FCSTD DOCUMENT  (FreeCAD 0.22R37543 (Git))
Label: FreeCAD_Symbol
License: All rights reserved
LicenseURL: https://en.wikipedia.org/wiki/All_rights_reserved
objects: Sketcher::SketchObject×1
note: 1 computed .brp shape members not serialized (recipe doc carries the construction recipe); baked Part::Feature solids carry a one-line shape summary decoded from their .brp

FEATURE [Sketcher::SketchObject] Sketch001  label="Logo_Sketch"
  FullyConstrained = true
  sketch-geometry (64):
    g0: LineSegment StartX=0 StartY=-4 StartZ=0 EndX=0 EndY=-24 EndZ=0
    g1: LineSegment StartX=0 StartY=-24 StartZ=0 EndX=8.05 EndY=-24 EndZ=0
    g2: LineSegment StartX=20 StartY=-7.99606 StartZ=0 EndX=20 EndY=0 EndZ=0
    g3: LineSegment StartX=20 StartY=0 StartZ=0 EndX=4 EndY=0 EndZ=0
    g4: ArcOfCircle CenterX=4 CenterY=-4 CenterZ=0 NormalX=0 NormalY=0 NormalZ=1 AngleXU=0 Radius=4 StartAngle=1.5708 EndAngle=3.14159
    g5: GeomPoint X=0 Y=0 Z=0
    g6: LineSegment StartX=4 StartY=0 StartZ=0 EndX=0 EndY=-4 EndZ=0
    g7: LineSegment StartX=4 StartY=-4 StartZ=0 EndX=4 EndY=-20 EndZ=0
    g8: LineSegment StartX=4 StartY=-20 StartZ=0 EndX=8 EndY=-20 EndZ=0
    g9: LineSegment StartX=8 StartY=-20 StartZ=0 EndX=8 EndY=-15 EndZ=0
    g10: LineSegment StartX=8 StartY=-15 StartZ=0 EndX=12 EndY=-15 EndZ=0
    g11: LineSegment StartX=12 StartY=-15 StartZ=0 EndX=12 EndY=-11 EndZ=0
    g12: LineSegment StartX=12 StartY=-11 StartZ=0 EndX=8 EndY=-11 EndZ=0
    g13: LineSegment StartX=8 StartY=-11 StartZ=0 EndX=8 EndY=-8 EndZ=0
    g14: LineSegment StartX=8 StartY=-8 StartZ=0 EndX=16 EndY=-8 EndZ=0
    g15: LineSegment StartX=16 StartY=-8 StartZ=0 EndX=16 EndY=-4 EndZ=0
    g16: LineSegment StartX=16 StartY=-4 StartZ=0 EndX=4 EndY=-4 EndZ=0
    g17: LineSegment StartX=19.7114 StartY=-8.56237 StartZ=0 EndX=17.5386 EndY=-10.1411 EndZ=0
    g18: LineSegment StartX=17.25 StartY=-10.7074 StartZ=0 EndX=17.25 EndY=-11.2926 EndZ=0
    g19: LineSegment StartX=17.5386 StartY=-11.8589 StartZ=0 EndX=19.4339 EndY=-13.236 EndZ=0
    g20: LineSegment StartX=19.6882 StartY=-14.0186 StartZ=0 EndX=19.0393 EndY=-16.0158 EndZ=0
    g21: LineSegment StartX=18.3735 StartY=-16.4995 StartZ=0 EndX=16.0307 EndY=-16.4995 EndZ=0
    g22: LineSegment StartX=15.4644 StartY=-16.7881 StartZ=0 EndX=15.1204 EndY=-17.2615 EndZ=0
    g23: LineSegment StartX=15.021 StartY=-17.8893 StartZ=0 EndX=15.745 EndY=-20.1174 EndZ=0
    g24: LineSegment StartX=15.4907 StartY=-20.9 StartZ=0 EndX=13.7917 EndY=-22.1344 EndZ=0
    g25: LineSegment StartX=12.9688 StartY=-22.1344 StartZ=0 EndX=11.0735 EndY=-20.7573 EndZ=0
    g26: LineSegment StartX=10.4457 StartY=-20.6579 StartZ=0 EndX=9.88913 EndY=-20.8388 EndZ=0
    g27: LineSegment StartX=9.4397 StartY=-21.2882 StartZ=0 EndX=8.71574 EndY=-23.5163 EndZ=0
    g28: LineSegment StartX=7 StartY=-11 StartZ=0 EndX=19.3637 EndY=-15.0172 EndZ=0
    g29: LineSegment StartX=7 StartY=-11 StartZ=0 EndX=19.3637 EndY=-6.98278 EndZ=0
    g30: LineSegment StartX=7 StartY=-11 StartZ=0 EndX=14.6412 EndY=-21.5172 EndZ=0
    g31: LineSegment StartX=7 StartY=-11 StartZ=0 EndX=7 EndY=-24 EndZ=0
    g32: Circle CenterX=7 CenterY=-11 CenterZ=0 NormalX=0 NormalY=0 NormalZ=1 AngleXU=0 Radius=13
    g33: LineSegment StartX=7 StartY=-11 StartZ=0 EndX=20 EndY=-11 EndZ=0
    g34: LineSegment StartX=7 StartY=-11 StartZ=0 EndX=17.5172 EndY=-18.6412 EndZ=0
    g35: LineSegment StartX=7 StartY=-11 StartZ=0 EndX=11.0172 EndY=-23.3637 EndZ=0
    g36: GeomPoint X=10.1674 Y=-20.7483 Z=0
    g37: Circle CenterX=7 CenterY=-11 CenterZ=0 NormalX=0 NormalY=0 NormalZ=1 AngleXU=0 Radius=10.25
    g38: ArcOfCircle CenterX=19.3 CenterY=-7.99606 CenterZ=0 NormalX=0 NormalY=0 NormalZ=1 AngleXU=0 Radius=0.7 StartAngle=5.34071 EndAngle=6.28319
    g39: GeomPoint X=20 Y=-8.35273 Z=0
    g40: ArcOfCircle CenterX=19.0225 CenterY=-13.8023 CenterZ=0 NormalX=0 NormalY=0 NormalZ=1 AngleXU=0 Radius=0.7 StartAngle=5.96903 EndAngle=7.22566
    g41: GeomPoint X=19.8454 Y=-13.5349 Z=0
    g42: ArcOfCircle CenterX=17.95 CenterY=-11.2926 CenterZ=0 NormalX=0 NormalY=0 NormalZ=1 AngleXU=0 Radius=0.7 StartAngle=3.14159 EndAngle=4.08407
    g43: GeomPoint X=17.25 Y=-11.6493 Z=0
    g44: ArcOfCircle CenterX=17.95 CenterY=-10.7074 CenterZ=0 NormalX=0 NormalY=0 NormalZ=1 AngleXU=0 Radius=0.7 StartAngle=2.19911 EndAngle=3.14159
    g45: GeomPoint X=17.25 Y=-10.3507 Z=0
    g46: ArcOfCircle CenterX=18.3735 CenterY=-15.7995 CenterZ=0 NormalX=0 NormalY=0 NormalZ=1 AngleXU=0 Radius=0.7 StartAngle=4.71239 EndAngle=5.96903
    g47: GeomPoint X=18.8821 Y=-16.4995 Z=0
    g48: ArcOfCircle CenterX=16.0307 CenterY=-17.1995 CenterZ=0 NormalX=0 NormalY=0 NormalZ=1 AngleXU=0 Radius=0.7 StartAngle=1.5708 EndAngle=2.51327
    g49: GeomPoint X=15.6741 Y=-16.4995 Z=0
    g50: ArcOfCircle CenterX=15.6867 CenterY=-17.673 CenterZ=0 NormalX=0 NormalY=0 NormalZ=1 AngleXU=0 Radius=0.7 StartAngle=2.51327 EndAngle=3.45575
    g51: GeomPoint X=14.9108 Y=-17.5501 Z=0
    g52: ArcOfCircle CenterX=15.0792 CenterY=-20.3337 CenterZ=0 NormalX=0 NormalY=0 NormalZ=1 AngleXU=0 Radius=0.7 StartAngle=5.34071 EndAngle=6.59734
    g53: GeomPoint X=15.9021 Y=-20.6011 Z=0
    g54: ArcOfCircle CenterX=13.3803 CenterY=-21.5681 CenterZ=0 NormalX=0 NormalY=0 NormalZ=1 AngleXU=0 Radius=0.7 StartAngle=4.08407 EndAngle=5.34071
    g55: GeomPoint X=13.3803 Y=-22.4333 Z=0
    g56: ArcOfCircle CenterX=10.662 CenterY=-21.3236 CenterZ=0 NormalX=0 NormalY=0 NormalZ=1 AngleXU=0 Radius=0.7 StartAngle=0.942478 EndAngle=1.88496
    g57: GeomPoint X=10.7849 Y=-20.5477 Z=0
    g58: ArcOfCircle CenterX=10.1054 CenterY=-21.5045 CenterZ=0 NormalX=0 NormalY=0 NormalZ=1 AngleXU=0 Radius=0.7 StartAngle=1.88496 EndAngle=2.82743
    g59: GeomPoint X=9.54992 Y=-20.949 Z=0
    g60: ArcOfCircle CenterX=8.05 CenterY=-23.3 CenterZ=0 NormalX=0 NormalY=0 NormalZ=1 AngleXU=0 Radius=0.7 StartAngle=4.71239 EndAngle=5.96903
    g61: GeomPoint X=8.55858 Y=-24 Z=0
    g62: GeomPoint X=17.25 Y=-11 Z=0
    g63: GeomPoint X=15.2924 Y=-17.0248 Z=0
  constraints (153):
    c: Coincident(g0,g1)
    c: Coincident(g2,g3)
    c: Vertical(g0)
    c: Vertical(g2)
    c: Horizontal(g1)
    c: Horizontal(g3)
    c: Coincident(g5,g-1)
    c: DistanceY(g0,g5) = 24
    c: DistanceX(g5,g3) = 20
    c: PointOnObject(g5,g0)
    c: PointOnObject(g5,g3)
    c: Tangent(g0,g4) = -1.5708
    c: Tangent(g3,g4) = -1.5708
    c: Coincident(g6,g0)
    c: Coincident(g6,g3)
    c: DistanceX(g-1,g3) = 4
    c: Coincident(g7,g4)
    c: Vertical(g7)
    c: Coincident(g7,g8)
    c: Horizontal(g8)
    c: Coincident(g8,g9)
    c: Vertical(g9)
    c: Coincident(g9,g10)
    c: Coincident(g10,g11)
    c: Coincident(g11,g12)
    c: Coincident(g12,g13)
    c: Coincident(g13,g14)
    c: Coincident(g14,g15)
    c: Coincident(g15,g16)
    c: Coincident(g16,g7)
    c: Horizontal(g10)
    c: Vertical(g11)
    c: Horizontal(g12)
    c: Vertical(g13)
    c: Horizontal(g14)
    c: Vertical(g15)
    c: Horizontal(g16)
    c: DistanceX(g16,g16) = 12
    c: DistanceY(g15,g15) = 4
    c: DistanceY(g11,g11) = 4
    c: DistanceX(g8,g8) = 4
    c: DistanceY(g7,g7) = 16
    c: Vertical(g9,g12)
    c: DistanceY(g13,g13) = 3
    c: DistanceX(g10,g10) = 4
    c: Coincident(g29,g28)
    c: Coincident(g30,g28)
    c: Coincident(g31,g28)
    c: Vertical(g31)
    c: Horizontal(g28,g12)
    c: Distance(g28,g12) = 1
    c: Angle(g31,g30) = 0.628319
    c: Angle(g30,g28) = 0.628319
    c: Angle(g28,g29) = 0.628319
    c: Coincident(g32,g28)
    c: PointOnObject(g31,g32)
    c: PointOnObject(g30,g32)
    c: PointOnObject(g28,g32)
    c: PointOnObject(g29,g32)
    c: Coincident(g33,g28)
    c: PointOnObject(g33,g32)
    c: Coincident(g34,g28)
    c: PointOnObject(g34,g32)
    c: Angle(g30,g34) = 0.314159
    c: Coincident(g35,g28)
    c: PointOnObject(g35,g32)
    c: Angle(g31,g35) = 0.314159
    c: PointOnObject(g36,g35)
    c: Coincident(g37,g28)
    c: PointOnObject(g36,g37)
    c: PointOnObject(g28,g20)
    c: PointOnObject(g36,g26)
    c: Diameter(g37) = 20.5
    c: PointOnObject(g39,g2)
    c: PointOnObject(g39,g17)
    c: Tangent(g2,g38) = -1.5708
    c: Tangent(g17,g38) = 1.5708
    c: PointOnObject(g41,g19)
    c: PointOnObject(g41,g20)
    c: Tangent(g19,g40) = 1.5708
    c: Tangent(g20,g40) = 1.5708
    c: PointOnObject(g43,g19)
    c: PointOnObject(g43,g18)
    c: Tangent(g19,g42) = -1.5708
    c: Tangent(g18,g42) = -1.5708
    c: PointOnObject(g45,g18)
    c: PointOnObject(g45,g17)
    c: Tangent(g18,g44) = -1.5708
    c: Tangent(g17,g44) = -1.5708
    c: PointOnObject(g47,g20)
    c: PointOnObject(g47,g21)
    c: Tangent(g20,g46) = 1.5708
    c: Tangent(g21,g46) = 1.5708
    c: PointOnObject(g49,g21)
    c: PointOnObject(g49,g22)
    c: Tangent(g21,g48) = -1.5708
    c: Tangent(g22,g48) = -1.5708
    c: PointOnObject(g51,g22)
    c: PointOnObject(g51,g23)
    c: Tangent(g22,g50) = -1.5708
    c: Tangent(g23,g50) = -1.5708
    c: PointOnObject(g53,g23)
    c: PointOnObject(g53,g24)
    c: Tangent(g23,g52) = 1.5708
    c: Tangent(g24,g52) = 1.5708
    c: PointOnObject(g55,g24)
    c: PointOnObject(g55,g25)
    c: Tangent(g24,g54) = 1.5708
    c: Tangent(g25,g54) = 1.5708
    c: PointOnObject(g57,g25)
    c: PointOnObject(g57,g26)
    c: Tangent(g25,g56) = -1.5708
    c: Tangent(g26,g56) = -1.5708
    c: PointOnObject(g59,g26)
    c: PointOnObject(g59,g27)
    c: Tangent(g26,g58) = -1.5708
    c: Tangent(g27,g58) = -1.5708
    c: PointOnObject(g61,g27)
    c: PointOnObject(g61,g1)
    c: Tangent(g27,g60) = 1.5708
    c: Tangent(g1,g60) = -1.5708
    c: Radius(g60) = 0.7
    c: Equal(g60,g58)
    c: Equal(g60,g56)
    c: Equal(g60,g54)
    c: Equal(g60,g52)
    c: Equal(g60,g50)
    c: Equal(g60,g48)
    c: Equal(g60,g46)
    c: Equal(g40,g60)
    c: Equal(g42,g60)
    c: Equal(g60,g44)
    c: Equal(g38,g60)
    c: Symmetric(g47,g41,g28)
    c: Symmetric(g53,g55,g30)
    c: Symmetric(g59,g57,g35)
    c: Symmetric(g51,g49,g34)
    c: Symmetric(g45,g43,g33)
    c: Angle(g28,g33) = 0.314159
    c: PointOnObject(g31,g1)
    c: Equal(g27,g25)
    c: PointOnObject(g62,g33)
    c: PointOnObject(g62,g37)
    c: PointOnObject(g62,g18)
    c: PointOnObject(g63,g34)
    c: PointOnObject(g63,g37)
    c: PointOnObject(g63,g22)
    c: Angle(g33,g17) = 0.628319
    c: Symmetric(g47,g53,g34)
    c: Angle(g30,g25) = 0.314159
    c: Equal(g26,g22)
    c: Equal(g26,g18)
    c: Distance(g20,g20) = 2.1
